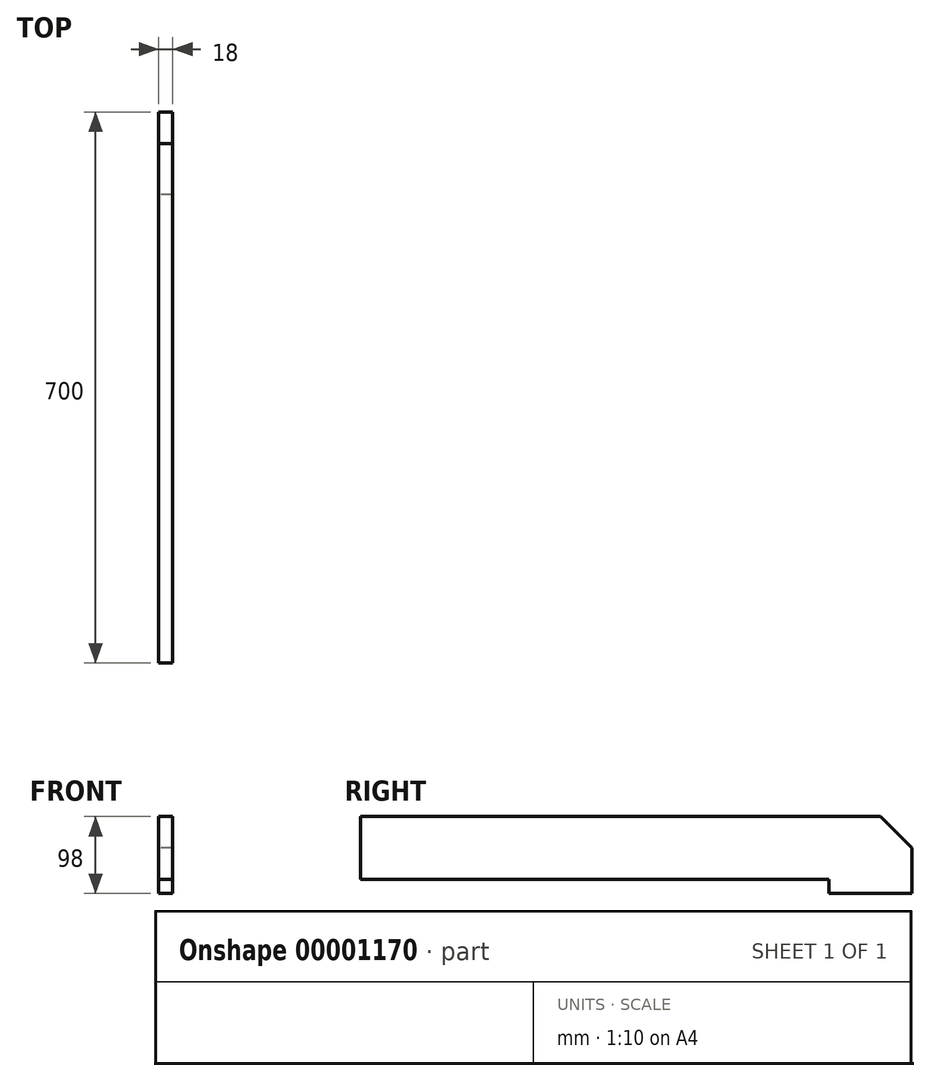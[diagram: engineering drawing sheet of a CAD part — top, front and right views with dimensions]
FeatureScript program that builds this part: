
annotation { "Feature Type Name" : "Feature", "Feature Type Description" : "" }
export const myFeature = defineFeature(function(context is Context, id is Id, definition is map)
    precondition{}
    {
        {
            var Q0;
            Q0=qCreatedBy(makeId("Right.planeOp"),FACE);
            var sketch = newSketch(context, id + "F0", { "sketchPlane" : qUnion([Q0])});
            skLineSegment(sketch, "E0", {"start": v(0, 0) * mm, "end": v(0, 80) * mm});
            skLineSegment(sketch, "E1", {"start": v(0, 80) * mm, "end": v(660, 80) * mm});
            skLineSegment(sketch, "E2", {"start": v(0, 0) * mm, "end": v(595, 0) * mm});
            skLineSegment(sketch, "E3", {"start": v(595, 0) * mm, "end": v(595, -18) * mm});
            skLineSegment(sketch, "E4", {"start": v(595, -18) * mm, "end": v(700, -18) * mm});
            skLineSegment(sketch, "E5", {"start": v(700, -18) * mm, "end": v(700, 40) * mm});
            skLineSegment(sketch, "E6", {"start": v(700, 40) * mm, "end": v(660, 80) * mm});
            skSolve(sketch);
        }
        {
            var Q0;
            Q0 = qSketchRegion(id + "F0", true);
            extrude(context, id + "F1", {"entities" : qUnion([Q0]), "depth" : 18 * mm});
        }
    });
